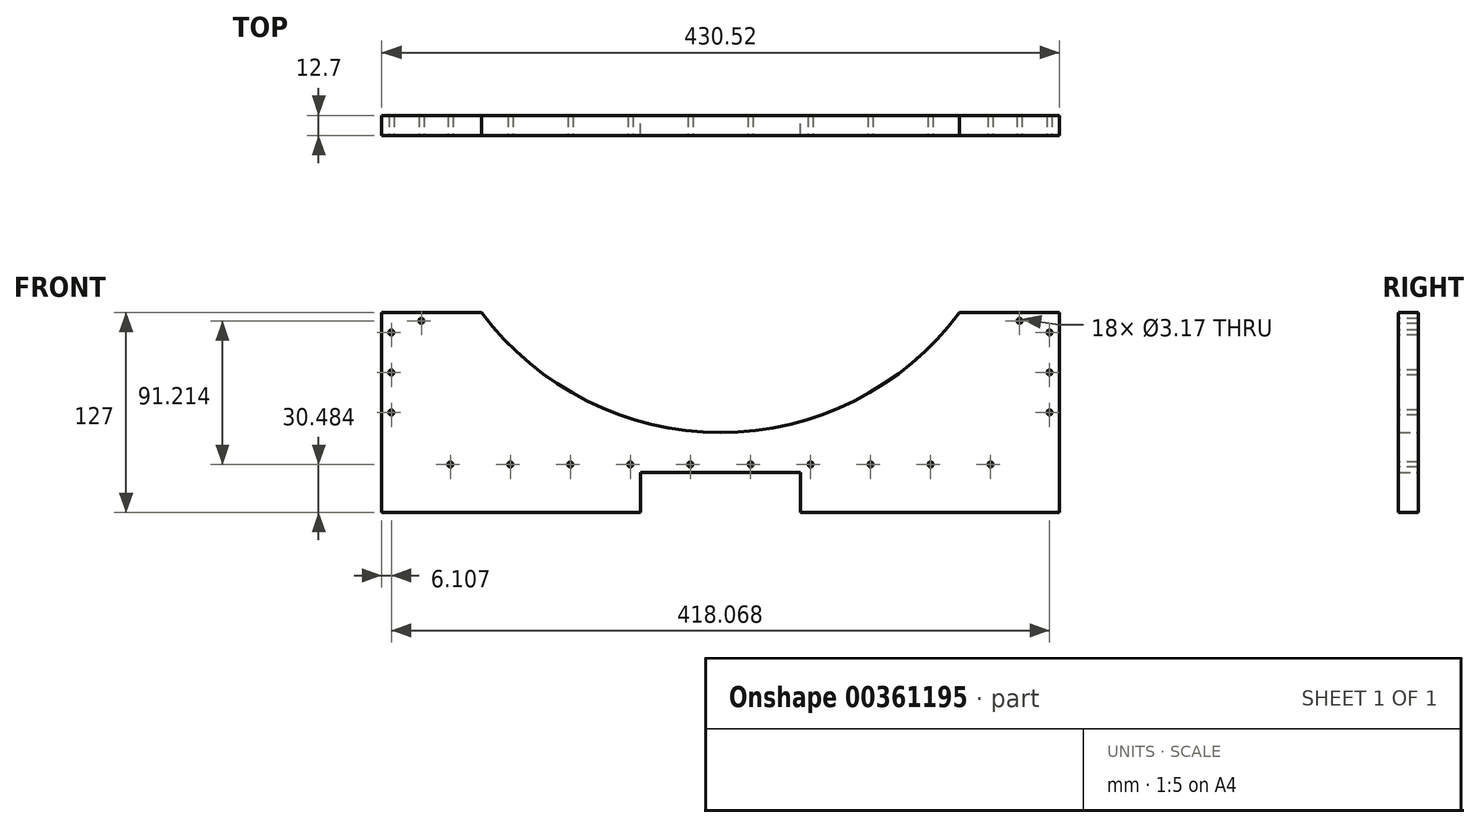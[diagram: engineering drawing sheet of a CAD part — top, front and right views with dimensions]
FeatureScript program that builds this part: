
annotation { "Feature Type Name" : "Feature", "Feature Type Description" : "" }
export const myFeature = defineFeature(function(context is Context, id is Id, definition is map)
    precondition{}
    {
        {
            var Q0;
            Q0=qCreatedBy(makeId("Front.planeOp"),FACE);
            var sketch = newSketch(context, id + "F0", { "sketchPlane" : qUnion([Q0])});
            skLineSegment(sketch, "E0.bottom", {"start": v(-194.5, -21.8) * mm, "end": v(-131, -21.8) * mm});
            skLineSegment(sketch, "E0.top", {"start": v(-194.5, -148.8) * mm, "end": v(-30.04, -148.8) * mm});
            skLineSegment(sketch, "E0.left", {"start": v(-194.5, -21.8) * mm, "end": v(-194.5, -148.8) * mm});
            skLineSegment(sketch, "E0.right", {"start": v(236.02, -21.8) * mm, "end": v(236.02, -148.8) * mm});
            skLineSegment(sketch, "E1.top", {"start": v(-30.04, -123.4) * mm, "end": v(71.56, -123.4) * mm});
            skLineSegment(sketch, "E1.left", {"start": v(-30.04, -148.8) * mm, "end": v(-30.04, -123.4) * mm});
            skLineSegment(sketch, "E1.right", {"start": v(71.56, -148.8) * mm, "end": v(71.56, -123.4) * mm});
            skLineSegment(sketch, "E2.trimOffspring", {"start": v(172.52, -21.8) * mm, "end": v(236.02, -21.8) * mm});
            skLineSegment(sketch, "E3.trimOffspring", {"start": v(71.56, -148.8) * mm, "end": v(236.02, -148.8) * mm});
            skArc(sketch, "E4", {"start": v(-131, -21.8) * mm, "mid": v(20.76, -98) * mm, "end": v(172.52, -21.8) * mm});
            skSolve(sketch);
        }
        {
            var Q0;
            Q0=makeQuery(id+"F0.imprint","IMPRINT",FACE,{"disambiguationData":[TD([[makeQuery(id+"F0.imprint","IMPRINT",EDGE,{"derivedFrom":sQuery(id+"F0.wireOp",EDGE,"E0.bottom")}),-1.0]])]});
            extrude(context, id + "F1", {"entities" : qUnion([Q0]), "depth" : 12.7 * mm});
        }
        {
            var Q0;
            Q0=makeQuery(id+"F1.opExtrude","CAP_FACE",FACE,{"disambiguationData":[OSD([sQuery(id+"F0.wireOp",EDGE,"E0.bottom"),sQuery(id+"F0.wireOp",EDGE,"E0.top"),sQuery(id+"F0.wireOp",EDGE,"E0.left"),sQuery(id+"F0.wireOp",EDGE,"E0.right"),sQuery(id+"F0.wireOp",EDGE,"E1.top"),sQuery(id+"F0.wireOp",EDGE,"E1.left"),sQuery(id+"F0.wireOp",EDGE,"E1.right"),sQuery(id+"F0.wireOp",EDGE,"E2.trimOffspring"),sQuery(id+"F0.wireOp",EDGE,"E3.trimOffspring"),sQuery(id+"F0.wireOp",EDGE,"E4")])],"isStart":false});
            var sketch = newSketch(context, id + "F2", { "sketchPlane" : qUnion([Q0])});
            skCircle(sketch, "E5", {"center": v(229.67, -34.5) * mm, "radius": 3.18 * mm});
            skCircle(sketch, "E6", {"center": v(229.67, -59.9) * mm, "radius": 3.18 * mm});
            skCircle(sketch, "E7", {"center": v(229.67, -85.3) * mm, "radius": 3.18 * mm});
            skCircle(sketch, "E8", {"center": v(77.91, -118.32) * mm, "radius": 3.18 * mm});
            skLineSegment(sketch, "E9", {"start": v(229.67, -118.32) * mm, "end": v(20.76, -118.32) * mm, "construction": true});
            skLineSegment(sketch, "E10", {"start": v(229.67, -118.32) * mm, "end": v(229.67, -27.1) * mm, "construction": true});
            skCircle(sketch, "E11", {"center": v(116.01, -118.32) * mm, "radius": 3.18 * mm});
            skCircle(sketch, "E12", {"center": v(154.11, -118.32) * mm, "radius": 3.18 * mm});
            skCircle(sketch, "E13", {"center": v(192.21, -118.32) * mm, "radius": 3.18 * mm});
            skCircle(sketch, "E14", {"center": v(39.81, -118.32) * mm, "radius": 3.18 * mm});
            skCircle(sketch, "E15", {"center": v(229.67, -34.5) * mm, "radius": 1.59 * mm});
            skCircle(sketch, "E16", {"center": v(229.67, -59.9) * mm, "radius": 1.59 * mm});
            skCircle(sketch, "E17", {"center": v(229.67, -85.3) * mm, "radius": 1.6 * mm});
            skCircle(sketch, "E18", {"center": v(192.21, -118.32) * mm, "radius": 1.59 * mm});
            skCircle(sketch, "E19", {"center": v(154.11, -118.32) * mm, "radius": 1.6 * mm});
            skCircle(sketch, "E20", {"center": v(116.01, -118.32) * mm, "radius": 1.59 * mm});
            skCircle(sketch, "E21", {"center": v(77.91, -118.32) * mm, "radius": 1.59 * mm});
            skCircle(sketch, "E22", {"center": v(39.81, -118.32) * mm, "radius": 1.59 * mm});
            skCircle(sketch, "E23", {"center": v(210.62, -27.1) * mm, "radius": 3.18 * mm});
            skCircle(sketch, "E24", {"center": v(210.62, -27.1) * mm, "radius": 1.59 * mm});
            skLineSegment(sketch, "E25", {"start": v(20.64, -128.67) * mm, "end": v(20.64, -87.07) * mm, "construction": true});
            skCircle(sketch, "E26.MirrorC", {"center": v(-188.4, -34.5) * mm, "radius": 1.59 * mm});
            skCircle(sketch, "E27.MirrorC", {"center": v(-169.34, -27.1) * mm, "radius": 3.18 * mm});
            skCircle(sketch, "E28.MirrorC", {"center": v(-169.34, -27.1) * mm, "radius": 1.59 * mm});
            skCircle(sketch, "E29.MirrorC", {"center": v(-188.4, -34.5) * mm, "radius": 3.18 * mm});
            skCircle(sketch, "E30.MirrorC", {"center": v(-36.63, -118.32) * mm, "radius": 3.18 * mm});
            skCircle(sketch, "E31.MirrorC", {"center": v(-36.63, -118.32) * mm, "radius": 1.59 * mm});
            skCircle(sketch, "E32.MirrorC", {"center": v(-188.4, -85.3) * mm, "radius": 1.6 * mm});
            skCircle(sketch, "E33.MirrorC", {"center": v(-188.4, -59.9) * mm, "radius": 1.59 * mm});
            skCircle(sketch, "E34.MirrorC", {"center": v(1.47, -118.32) * mm, "radius": 3.18 * mm});
            skCircle(sketch, "E35.MirrorC", {"center": v(-150.93, -118.32) * mm, "radius": 3.18 * mm});
            skCircle(sketch, "E36.MirrorC", {"center": v(-112.83, -118.32) * mm, "radius": 3.18 * mm});
            skCircle(sketch, "E37.MirrorC", {"center": v(-74.73, -118.32) * mm, "radius": 3.18 * mm});
            skCircle(sketch, "E38.MirrorC", {"center": v(-150.93, -118.32) * mm, "radius": 1.59 * mm});
            skCircle(sketch, "E39.MirrorC", {"center": v(1.47, -118.32) * mm, "radius": 1.59 * mm});
            skCircle(sketch, "E40.MirrorC", {"center": v(-188.4, -85.3) * mm, "radius": 3.18 * mm});
            skCircle(sketch, "E41.MirrorC", {"center": v(-74.73, -118.32) * mm, "radius": 1.59 * mm});
            skCircle(sketch, "E42.MirrorC", {"center": v(-112.83, -118.32) * mm, "radius": 1.6 * mm});
            skCircle(sketch, "E43.MirrorC", {"center": v(-188.4, -59.9) * mm, "radius": 3.18 * mm});
            skLineSegment(sketch, "E44.MirrorCS", {"start": v(-188.4, -118.32) * mm, "end": v(-188.4, -27.1) * mm, "construction": true});
            skLineSegment(sketch, "E45.MirrorCS", {"start": v(-188.4, -118.32) * mm, "end": v(20.52, -118.32) * mm, "construction": true});
            skLineSegment(sketch, "E46", {"start": v(-130.6, -27.1) * mm, "end": v(-188.4, -27.1) * mm, "construction": true});
            skLineSegment(sketch, "E47", {"start": v(229.67, -27.1) * mm, "end": v(171.89, -27.1) * mm, "construction": true});
            skArc(sketch, "E48", {"start": v(-130.6, -27.1) * mm, "mid": v(20.64, -103.47) * mm, "end": v(171.89, -27.1) * mm});
            skSolve(sketch);
        }
        {
            var Q0;
            Q0=sQuery(id+"F2.wireOp",VERTEX,"E5.center");
            var Q1;
            Q1=sQuery(id+"F2.wireOp",VERTEX,"E16.center");
            var Q2;
            Q2=sQuery(id+"F2.wireOp",VERTEX,"E17.center");
            var Q3;
            Q3=sQuery(id+"F2.wireOp",VERTEX,"E18.center");
            var Q4;
            Q4=sQuery(id+"F2.wireOp",VERTEX,"E19.center");
            var Q5;
            Q5=sQuery(id+"F2.wireOp",VERTEX,"E20.center");
            var Q6;
            Q6=sQuery(id+"F2.wireOp",VERTEX,"E21.center");
            var Q7;
            Q7=sQuery(id+"F2.wireOp",VERTEX,"E14.center");
            var Q8;
            Q8=sQuery(id+"F2.wireOp",VERTEX,"E23.center");
            var Q9;
            Q9=sQuery(id+"F2.wireOp",VERTEX,"E39.MirrorC.center");
            var Q10;
            Q10=sQuery(id+"F2.wireOp",VERTEX,"E30.MirrorC.center");
            var Q11;
            Q11=sQuery(id+"F2.wireOp",VERTEX,"E41.MirrorC.center");
            var Q12;
            Q12=sQuery(id+"F2.wireOp",VERTEX,"E36.MirrorC.center");
            var Q13;
            Q13=sQuery(id+"F2.wireOp",VERTEX,"E35.MirrorC.center");
            var Q14;
            Q14=sQuery(id+"F2.wireOp",VERTEX,"E32.MirrorC.center");
            var Q15;
            Q15=sQuery(id+"F2.wireOp",VERTEX,"E43.MirrorC.center");
            var Q16;
            Q16=sQuery(id+"F2.wireOp",VERTEX,"E29.MirrorC.center");
            var Q17;
            Q17=sQuery(id+"F2.wireOp",VERTEX,"E28.MirrorC.center");
            var Q18;
            Q18=makeQuery(id+"F1.opExtrude","SWEPT_BODY",BODY,{"disambiguationData":[OSD([sQuery(id+"F0.wireOp",EDGE,"E0.bottom"),sQuery(id+"F0.wireOp",EDGE,"E0.top"),sQuery(id+"F0.wireOp",EDGE,"E0.left"),sQuery(id+"F0.wireOp",EDGE,"E0.right"),sQuery(id+"F0.wireOp",EDGE,"E1.top"),sQuery(id+"F0.wireOp",EDGE,"E1.left"),sQuery(id+"F0.wireOp",EDGE,"E1.right"),sQuery(id+"F0.wireOp",EDGE,"E2.trimOffspring"),sQuery(id+"F0.wireOp",EDGE,"E3.trimOffspring"),sQuery(id+"F0.wireOp",EDGE,"E4")])]});
            hole(context, id + "F3", {"style" : HoleStyle.SIMPLE, "endStyle" : HoleEndStyle.THROUGH, "holeDiameter" : 3.17 * mm, "isTappedThrough" : true, "tappedDepth" : 12.7 * mm, "tapClearance" : 3, "locations" : qUnion([Q0, Q1, Q2, Q3, Q4, Q5, Q6, Q7, Q8, Q9, Q10, Q11, Q12, Q13, Q14, Q15, Q16, Q17]), "scope" : qUnion([Q18])});
        }
    });
